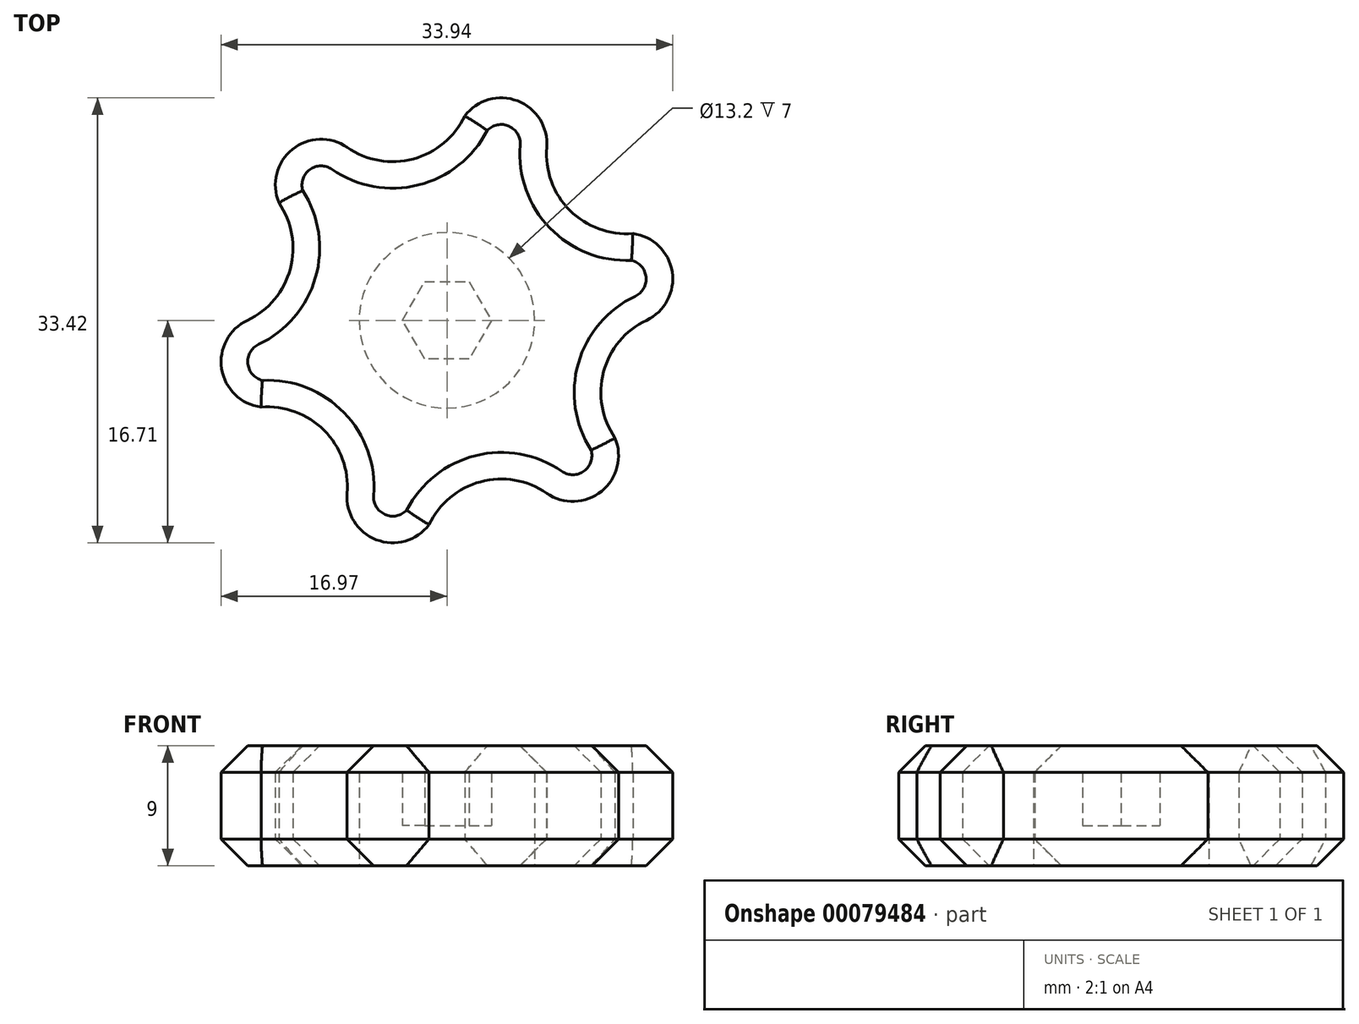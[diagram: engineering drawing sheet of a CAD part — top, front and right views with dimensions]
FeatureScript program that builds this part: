
annotation { "Feature Type Name" : "Feature", "Feature Type Description" : "" }
export const myFeature = defineFeature(function(context is Context, id is Id, definition is map)
    precondition{}
    {
        {
            var Q0;
            Q0=qCreatedBy(makeId("Top.planeOp"),FACE);
            var sketch = newSketch(context, id + "F0", { "sketchPlane" : qUnion([Q0])});
            skCircle(sketch, "E0.cCircle", {"center": v(0, 0) * mm, "radius": 2.9 * mm, "construction": true});
            skLineSegment(sketch, "E0.0", {"start": v(-3.35, 0) * mm, "end": v(-1.67, 2.9) * mm});
            skLineSegment(sketch, "E0.1", {"start": v(-1.67, 2.9) * mm, "end": v(1.67, 2.9) * mm});
            skLineSegment(sketch, "E0.2", {"start": v(1.67, 2.9) * mm, "end": v(3.35, 0) * mm});
            skLineSegment(sketch, "E0.3", {"start": v(3.35, 0) * mm, "end": v(1.67, -2.9) * mm});
            skLineSegment(sketch, "E0.4", {"start": v(1.67, -2.9) * mm, "end": v(-1.67, -2.9) * mm});
            skLineSegment(sketch, "E0.5", {"start": v(-1.67, -2.9) * mm, "end": v(-3.35, 0) * mm});
            skPoint(sketch, "E0.0.midPoint", {"position": v(-2.51, 1.45) * mm});
            skCircle(sketch, "E1", {"center": v(0, 0) * mm, "radius": 6.6 * mm});
            skArc(sketch, "E2", {"start": v(-7.5, 13) * mm, "mid": v(-11.62, 12.84) * mm, "end": v(-12.63, 8.84) * mm});
            skArc(sketch, "E3", {"start": v(-7.5, 13) * mm, "mid": v(-2.53, 12.13) * mm, "end": v(1.34, 15.36) * mm});
            skArc(sketch, "E4.1.0", {"start": v(-15, 0) * mm, "mid": v(-16.93, -3.65) * mm, "end": v(-13.97, -6.52) * mm});
            skArc(sketch, "E4.1.1", {"start": v(-15, 0) * mm, "mid": v(-11.77, 3.87) * mm, "end": v(-12.63, 8.84) * mm});
            skArc(sketch, "E4.2.0", {"start": v(-7.5, -13) * mm, "mid": v(-5.3, -16.48) * mm, "end": v(-1.34, -15.36) * mm});
            skArc(sketch, "E4.2.1", {"start": v(-7.5, -13) * mm, "mid": v(-9.24, -8.26) * mm, "end": v(-13.97, -6.52) * mm});
            skArc(sketch, "E4.3.0", {"start": v(7.5, -13) * mm, "mid": v(11.62, -12.84) * mm, "end": v(12.63, -8.84) * mm});
            skArc(sketch, "E4.3.1", {"start": v(7.5, -13) * mm, "mid": v(2.53, -12.13) * mm, "end": v(-1.34, -15.36) * mm});
            skArc(sketch, "E4.4.0", {"start": v(15, 0) * mm, "mid": v(16.93, 3.65) * mm, "end": v(13.97, 6.52) * mm});
            skArc(sketch, "E4.4.1", {"start": v(15, 0) * mm, "mid": v(11.77, -3.87) * mm, "end": v(12.63, -8.84) * mm});
            skArc(sketch, "E4.5.0", {"start": v(7.5, 13) * mm, "mid": v(5.3, 16.48) * mm, "end": v(1.34, 15.36) * mm});
            skArc(sketch, "E4.5.1", {"start": v(7.5, 13) * mm, "mid": v(9.24, 8.26) * mm, "end": v(13.97, 6.52) * mm});
            skSolve(sketch);
        }
        {
            var Q0;
            Q0=makeQuery(id+"F0.imprint","IMPRINT",FACE,{"disambiguationData":[TD([[makeQuery(id+"F0.imprint","IMPRINT",EDGE,{"derivedFrom":sQuery(id+"F0.wireOp",EDGE,"E1")}),-1.0]])]});
            var Q1;
            Q1=makeQuery(id+"F0.imprint","IMPRINT",FACE,{"disambiguationData":[TD([[makeQuery(id+"F0.imprint","IMPRINT",EDGE,{"derivedFrom":sQuery(id+"F0.wireOp",EDGE,"E0.0")}),-1.0]])]});
            var Q2;
            Q2=makeQuery(id+"F0.imprint","IMPRINT",FACE,{"disambiguationData":[TD([[makeQuery(id+"F0.imprint","IMPRINT",EDGE,{"derivedFrom":sQuery(id+"F0.wireOp",EDGE,"E0.0")}),1.0]])]});
            extrude(context, id + "F1", {"entities" : qUnion([Q0, Q1, Q2]), "depth" : 9 * mm, "offsetDistance" : 25 * mm});
        }
        {
            var Q0;
            Q0=makeQuery(id+"F0.imprint","IMPRINT",FACE,{"disambiguationData":[TD([[makeQuery(id+"F0.imprint","IMPRINT",EDGE,{"derivedFrom":sQuery(id+"F0.wireOp",EDGE,"E0.0")}),1.0]])]});
            extrude(context, id + "F2", {"entities" : qUnion([Q0]), "operationType" : NewBodyOperationType.REMOVE, "depth" : 7 * mm, "offsetDistance" : 25 * mm});
        }
        {
            var Q0;
            Q0=makeQuery(id+"F1.opExtrude","CAP_EDGE",EDGE,{"disambiguationData":[OSD([sQuery(id+"F0.wireOp",EDGE,"E3")])],"isStart":true});
            var Q1;
            Q1=makeQuery(id+"F1.opExtrude","CAP_EDGE",EDGE,{"disambiguationData":[OSD([sQuery(id+"F0.wireOp",EDGE,"E4.5.0")])],"isStart":true});
            var Q2;
            Q2=makeQuery(id+"F1.opExtrude","CAP_EDGE",EDGE,{"disambiguationData":[OSD([sQuery(id+"F0.wireOp",EDGE,"E4.5.1")])],"isStart":true});
            var Q3;
            Q3=makeQuery(id+"F1.opExtrude","CAP_EDGE",EDGE,{"disambiguationData":[OSD([sQuery(id+"F0.wireOp",EDGE,"E4.4.0")])],"isStart":true});
            var Q4;
            Q4=makeQuery(id+"F1.opExtrude","CAP_EDGE",EDGE,{"disambiguationData":[OSD([sQuery(id+"F0.wireOp",EDGE,"E4.4.1")])],"isStart":true});
            var Q5;
            Q5=makeQuery(id+"F1.opExtrude","CAP_EDGE",EDGE,{"disambiguationData":[OSD([sQuery(id+"F0.wireOp",EDGE,"E4.3.1")])],"isStart":true});
            var Q6;
            Q6=makeQuery(id+"F1.opExtrude","CAP_EDGE",EDGE,{"disambiguationData":[OSD([sQuery(id+"F0.wireOp",EDGE,"E4.2.0")])],"isStart":true});
            var Q7;
            Q7=makeQuery(id+"F1.opExtrude","CAP_EDGE",EDGE,{"disambiguationData":[OSD([sQuery(id+"F0.wireOp",EDGE,"E4.2.1")])],"isStart":true});
            var Q8;
            Q8=makeQuery(id+"F1.opExtrude","CAP_EDGE",EDGE,{"disambiguationData":[OSD([sQuery(id+"F0.wireOp",EDGE,"E4.1.0")])],"isStart":true});
            var Q9;
            Q9=makeQuery(id+"F1.opExtrude","CAP_EDGE",EDGE,{"disambiguationData":[OSD([sQuery(id+"F0.wireOp",EDGE,"E4.1.1")])],"isStart":true});
            var Q10;
            Q10=makeQuery(id+"F1.opExtrude","CAP_EDGE",EDGE,{"disambiguationData":[OSD([sQuery(id+"F0.wireOp",EDGE,"E4.5.1")])],"isStart":false});
            var Q11;
            Q11=makeQuery(id+"F1.opExtrude","CAP_EDGE",EDGE,{"disambiguationData":[OSD([sQuery(id+"F0.wireOp",EDGE,"E4.5.0")])],"isStart":false});
            var Q12;
            Q12=makeQuery(id+"F1.opExtrude","CAP_EDGE",EDGE,{"disambiguationData":[OSD([sQuery(id+"F0.wireOp",EDGE,"E3")])],"isStart":false});
            var Q13;
            Q13=makeQuery(id+"F1.opExtrude","CAP_EDGE",EDGE,{"disambiguationData":[OSD([sQuery(id+"F0.wireOp",EDGE,"E2")])],"isStart":false});
            var Q14;
            Q14=makeQuery(id+"F1.opExtrude","CAP_EDGE",EDGE,{"disambiguationData":[OSD([sQuery(id+"F0.wireOp",EDGE,"E4.1.1")])],"isStart":false});
            var Q15;
            Q15=makeQuery(id+"F1.opExtrude","CAP_EDGE",EDGE,{"disambiguationData":[OSD([sQuery(id+"F0.wireOp",EDGE,"E4.1.0")])],"isStart":false});
            var Q16;
            Q16=makeQuery(id+"F1.opExtrude","CAP_EDGE",EDGE,{"disambiguationData":[OSD([sQuery(id+"F0.wireOp",EDGE,"E4.2.1")])],"isStart":false});
            var Q17;
            Q17=makeQuery(id+"F1.opExtrude","CAP_EDGE",EDGE,{"disambiguationData":[OSD([sQuery(id+"F0.wireOp",EDGE,"E4.2.0")])],"isStart":false});
            var Q18;
            Q18=makeQuery(id+"F1.opExtrude","CAP_EDGE",EDGE,{"disambiguationData":[OSD([sQuery(id+"F0.wireOp",EDGE,"E4.3.1")])],"isStart":false});
            var Q19;
            Q19=makeQuery(id+"F1.opExtrude","CAP_EDGE",EDGE,{"disambiguationData":[OSD([sQuery(id+"F0.wireOp",EDGE,"E4.3.0")])],"isStart":false});
            var Q20;
            Q20=makeQuery(id+"F1.opExtrude","CAP_EDGE",EDGE,{"disambiguationData":[OSD([sQuery(id+"F0.wireOp",EDGE,"E4.4.1")])],"isStart":false});
            var Q21;
            Q21=makeQuery(id+"F1.opExtrude","CAP_EDGE",EDGE,{"disambiguationData":[OSD([sQuery(id+"F0.wireOp",EDGE,"E4.4.0")])],"isStart":false});
            chamfer(context, id + "F3", {"entities" : qUnion([Q0, Q1, Q2, Q3, Q4, Q5, Q6, Q7, Q8, Q9, Q10, Q11, Q12, Q13, Q14, Q15, Q16, Q17, Q18, Q19, Q20, Q21]), "width" : 2 * mm, "tangentPropagation" : true});
        }
        {
            var Q0;
            Q0=makeQuery(id+"F0.imprint","IMPRINT",FACE,{"disambiguationData":[TD([[makeQuery(id+"F0.imprint","IMPRINT",EDGE,{"derivedFrom":sQuery(id+"F0.wireOp",EDGE,"E0.0")}),-1.0]])]});
            extrude(context, id + "F4", {"entities" : qUnion([Q0]), "operationType" : NewBodyOperationType.REMOVE, "depth" : 3 * mm, "offsetDistance" : 25 * mm});
        }
    });
